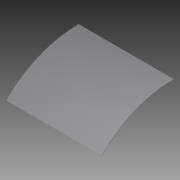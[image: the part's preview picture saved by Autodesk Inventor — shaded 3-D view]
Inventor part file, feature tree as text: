
AUTODESK INVENTOR PART (.ipt)
format: ipt  version: 2013 (Build 170138000, 138)  size: 77,312 bytes
history: native  units: in
note: dims shown in document units (in); Inventor stores cm internally (conversion verified against a paired STEP export)
features: extrude x1, sketch x1
ambient origin geometry x8: Origin, YZ Plane, XZ Plane, XY Plane, X Axis, Y Axis, Z Axis, Center Point
bodies: Solid1 (feature_tree)
feature tree (2):
  extrude  "Extrusion1"  Depth=0.0625in
  sketch  "Sketch1"  dims[d0=23.75in d1=0.0625in d2=45.0deg d3=11.125in d4=0.0in]
